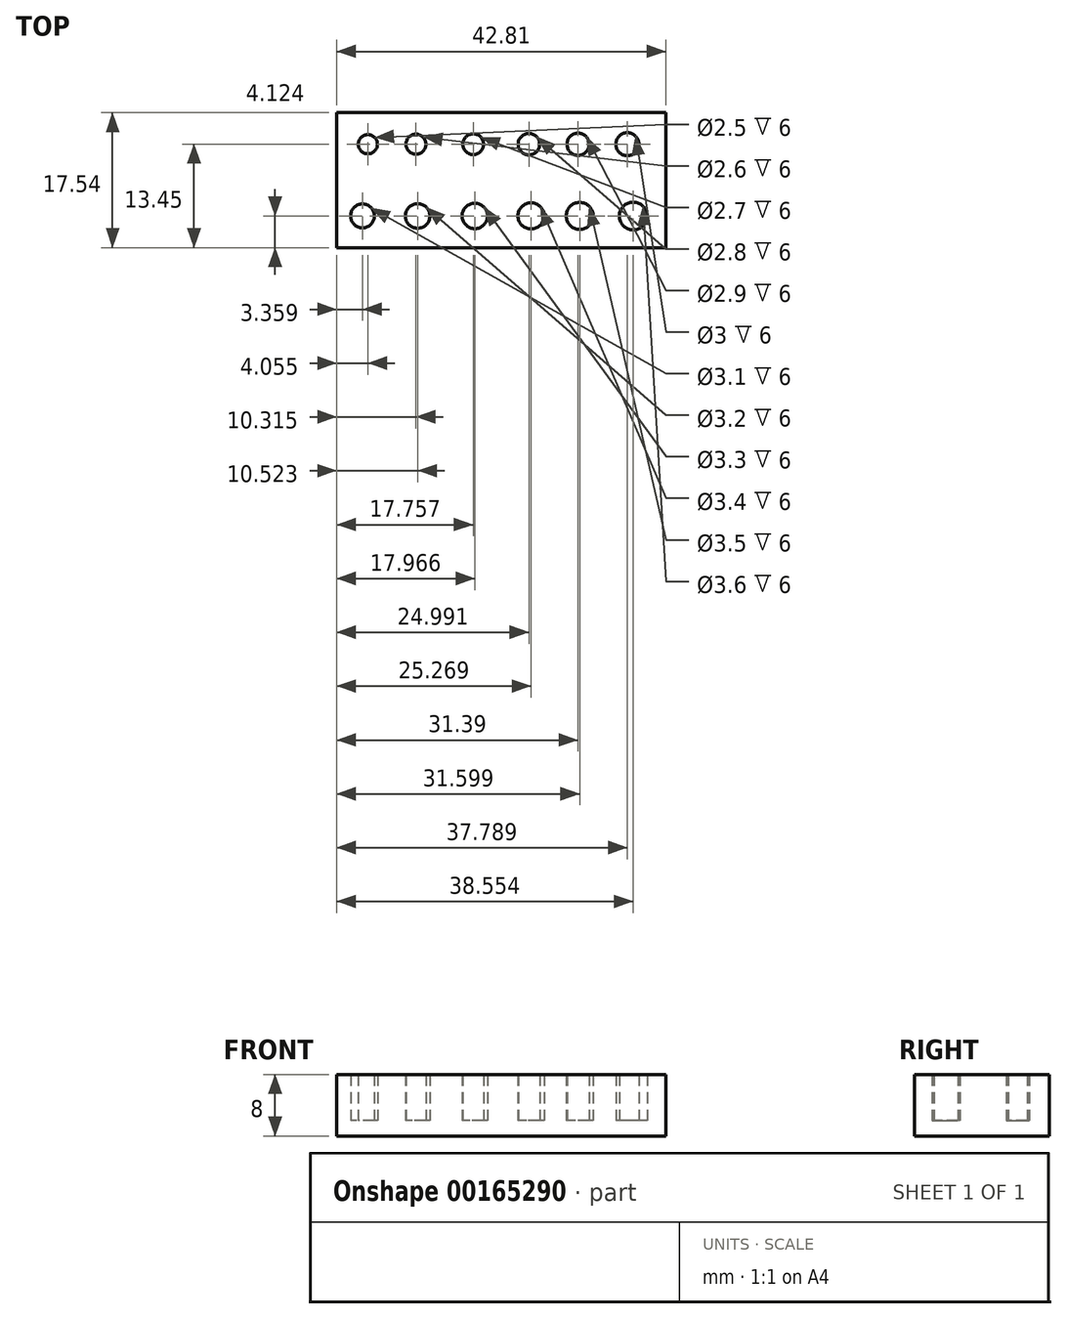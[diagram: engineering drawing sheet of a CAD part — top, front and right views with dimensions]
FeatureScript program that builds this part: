
annotation { "Feature Type Name" : "Feature", "Feature Type Description" : "" }
export const myFeature = defineFeature(function(context is Context, id is Id, definition is map)
    precondition{}
    {
        {
            var Q0;
            Q0=qCreatedBy(makeId("Top.planeOp"),FACE);
            var sketch = newSketch(context, id + "F0", { "sketchPlane" : qUnion([Q0])});
            skCircle(sketch, "E0", {"center": v(-43.26, 0) * mm, "radius": 1.25 * mm});
            skCircle(sketch, "E1", {"center": v(-37, 0) * mm, "radius": 1.3 * mm});
            skLineSegment(sketch, "E2", {"start": v(15.2, 0) * mm, "end": v(-45.26, 0) * mm, "construction": true});
            skCircle(sketch, "E3", {"center": v(-29.55, 0) * mm, "radius": 1.35 * mm});
            skCircle(sketch, "E4", {"center": v(-22.32, 0) * mm, "radius": 1.4 * mm});
            skCircle(sketch, "E5", {"center": v(-15.92, 0) * mm, "radius": 1.45 * mm});
            skCircle(sketch, "E6", {"center": v(-9.52, 0) * mm, "radius": 1.5 * mm});
            skCircle(sketch, "E7", {"center": v(-43.95, -9.33) * mm, "radius": 1.55 * mm});
            skCircle(sketch, "E8", {"center": v(-36.79, -9.33) * mm, "radius": 1.6 * mm});
            skCircle(sketch, "E9", {"center": v(-29.34, -9.33) * mm, "radius": 1.65 * mm});
            skCircle(sketch, "E10", {"center": v(-22.04, -9.33) * mm, "radius": 1.7 * mm});
            skCircle(sketch, "E11", {"center": v(-15.71, -9.33) * mm, "radius": 1.75 * mm});
            skLineSegment(sketch, "E12", {"start": v(-45.41, -9.33) * mm, "end": v(13.99, -9.33) * mm, "construction": true});
            skPoint(sketch, "E13", {"position": v(-15.03, 0) * mm});
            skLineSegment(sketch, "E14.bottom", {"start": v(-47.3, 4.1) * mm, "end": v(-4.5, 4.1) * mm});
            skLineSegment(sketch, "E14.top", {"start": v(-47.3, -13.45) * mm, "end": v(-4.5, -13.45) * mm});
            skLineSegment(sketch, "E14.left", {"start": v(-47.3, 4.1) * mm, "end": v(-47.3, -13.45) * mm});
            skLineSegment(sketch, "E14.right", {"start": v(-4.5, 4.1) * mm, "end": v(-4.5, -13.45) * mm});
            skCircle(sketch, "E15", {"center": v(-8.76, -9.33) * mm, "radius": 1.8 * mm});
            skSolve(sketch);
        }
        {
            var Q0;
            Q0=makeQuery(id+"F0.imprint","IMPRINT",FACE,{"disambiguationData":[TD([[makeQuery(id+"F0.imprint","IMPRINT",EDGE,{"derivedFrom":sQuery(id+"F0.wireOp",EDGE,"E0")}),-1.0]])]});
            extrude(context, id + "F1", {"entities" : qUnion([Q0]), "depth" : 8 * mm});
        }
        {
            var Q0;
            Q0=makeQuery(id+"F0.imprint","IMPRINT",FACE,{"disambiguationData":[TD([[makeQuery(id+"F0.imprint","IMPRINT",EDGE,{"derivedFrom":sQuery(id+"F0.wireOp",EDGE,"E7")}),1.0]])]});
            var Q1;
            Q1=makeQuery(id+"F0.imprint","IMPRINT",FACE,{"disambiguationData":[TD([[makeQuery(id+"F0.imprint","IMPRINT",EDGE,{"derivedFrom":sQuery(id+"F0.wireOp",EDGE,"E8")}),1.0]])]});
            var Q2;
            Q2=makeQuery(id+"F0.imprint","IMPRINT",FACE,{"disambiguationData":[TD([[makeQuery(id+"F0.imprint","IMPRINT",EDGE,{"derivedFrom":sQuery(id+"F0.wireOp",EDGE,"E9")}),1.0]])]});
            var Q3;
            Q3=makeQuery(id+"F0.imprint","IMPRINT",FACE,{"disambiguationData":[TD([[makeQuery(id+"F0.imprint","IMPRINT",EDGE,{"derivedFrom":sQuery(id+"F0.wireOp",EDGE,"E10")}),1.0]])]});
            var Q4;
            Q4=makeQuery(id+"F0.imprint","IMPRINT",FACE,{"disambiguationData":[TD([[makeQuery(id+"F0.imprint","IMPRINT",EDGE,{"derivedFrom":sQuery(id+"F0.wireOp",EDGE,"E11")}),1.0]])]});
            var Q5;
            Q5=makeQuery(id+"F0.imprint","IMPRINT",FACE,{"disambiguationData":[TD([[makeQuery(id+"F0.imprint","IMPRINT",EDGE,{"derivedFrom":sQuery(id+"F0.wireOp",EDGE,"E15")}),1.0]])]});
            var Q6;
            Q6=makeQuery(id+"F0.imprint","IMPRINT",FACE,{"disambiguationData":[TD([[makeQuery(id+"F0.imprint","IMPRINT",EDGE,{"derivedFrom":sQuery(id+"F0.wireOp",EDGE,"E6")}),1.0]])]});
            var Q7;
            Q7=makeQuery(id+"F0.imprint","IMPRINT",FACE,{"disambiguationData":[TD([[makeQuery(id+"F0.imprint","IMPRINT",EDGE,{"derivedFrom":sQuery(id+"F0.wireOp",EDGE,"E5")}),1.0]])]});
            var Q8;
            Q8=makeQuery(id+"F0.imprint","IMPRINT",FACE,{"disambiguationData":[TD([[makeQuery(id+"F0.imprint","IMPRINT",EDGE,{"derivedFrom":sQuery(id+"F0.wireOp",EDGE,"E4")}),1.0]])]});
            var Q9;
            Q9=makeQuery(id+"F0.imprint","IMPRINT",FACE,{"disambiguationData":[TD([[makeQuery(id+"F0.imprint","IMPRINT",EDGE,{"derivedFrom":sQuery(id+"F0.wireOp",EDGE,"E3")}),1.0]])]});
            var Q10;
            Q10=makeQuery(id+"F0.imprint","IMPRINT",FACE,{"disambiguationData":[TD([[makeQuery(id+"F0.imprint","IMPRINT",EDGE,{"derivedFrom":sQuery(id+"F0.wireOp",EDGE,"E1")}),1.0]])]});
            var Q11;
            Q11=makeQuery(id+"F0.imprint","IMPRINT",FACE,{"disambiguationData":[TD([[makeQuery(id+"F0.imprint","IMPRINT",EDGE,{"derivedFrom":sQuery(id+"F0.wireOp",EDGE,"E0")}),1.0]])]});
            var Q12;
            Q12=sQuery(id+"F0.wireOp",EDGE,"E12");
            extrude(context, id + "F2", {"entities" : qUnion([Q0, Q1, Q2, Q3, Q4, Q5, Q6, Q7, Q8, Q9, Q10, Q11]), "operationType" : NewBodyOperationType.ADD, "surfaceEntities" : qUnion([Q12]), "depth" : 2 * mm});
        }
    });
